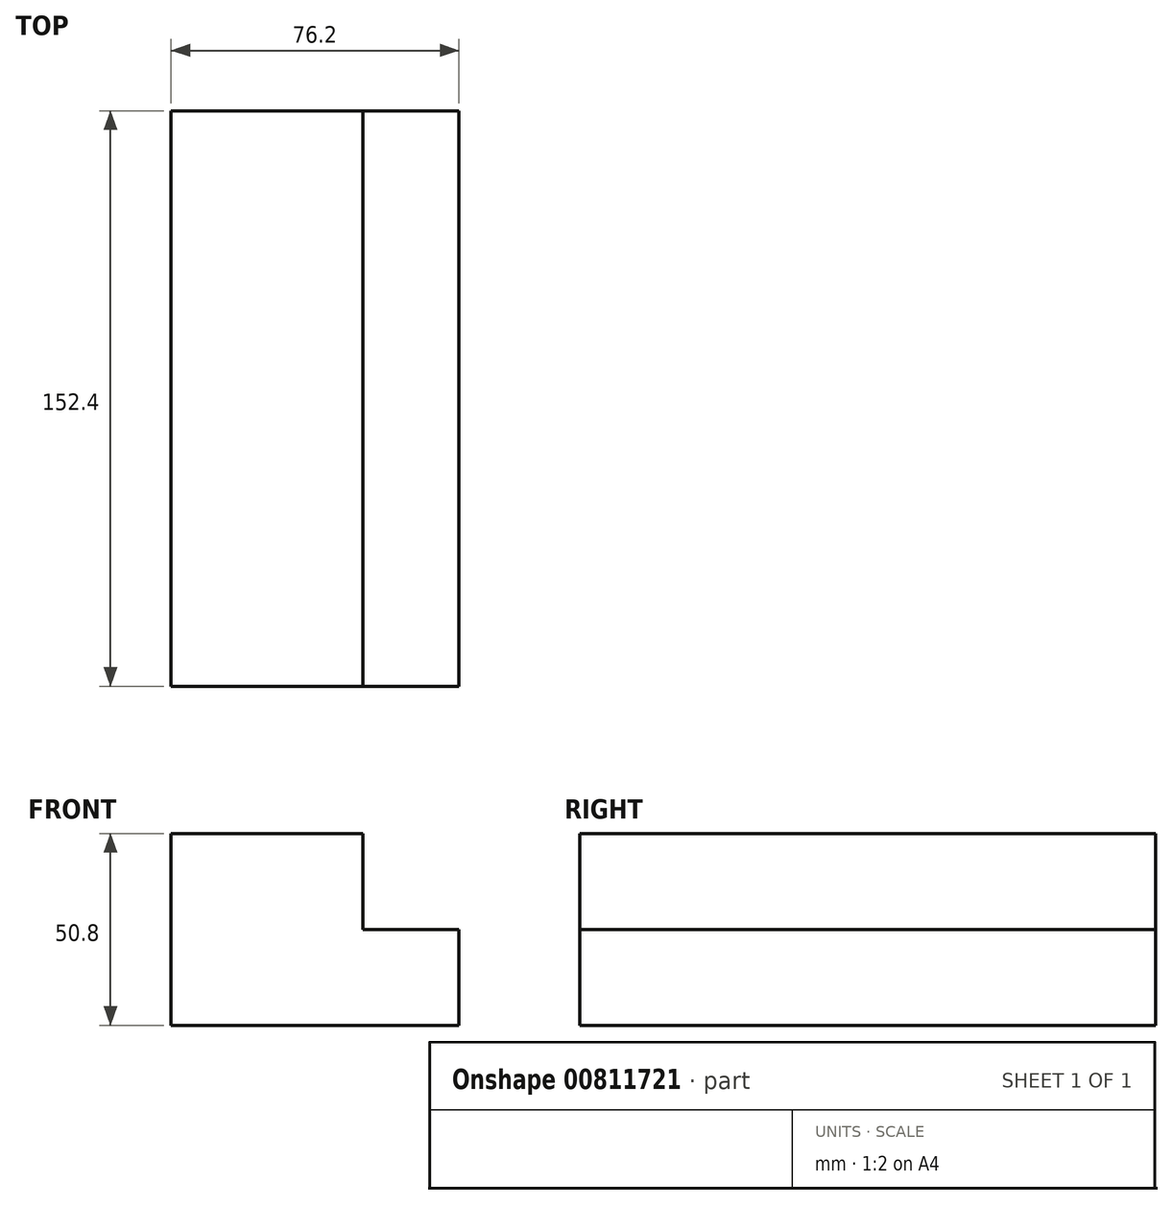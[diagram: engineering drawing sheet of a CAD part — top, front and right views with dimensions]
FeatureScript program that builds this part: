
annotation { "Feature Type Name" : "Feature", "Feature Type Description" : "" }
export const myFeature = defineFeature(function(context is Context, id is Id, definition is map)
    precondition{}
    {
        {
            var Q0;
            Q0=qCreatedBy(makeId("Front.planeOp"),FACE);
            var sketch = newSketch(context, id + "F0", { "sketchPlane" : qUnion([Q0])});
            skLineSegment(sketch, "E0", {"start": v(0, 0) * mm, "end": v(-76.2, 0) * mm});
            skLineSegment(sketch, "E1", {"start": v(-76.2, 0) * mm, "end": v(-76.2, 50.8) * mm});
            skLineSegment(sketch, "E2", {"start": v(-76.2, 50.8) * mm, "end": v(-25.4, 50.8) * mm});
            skLineSegment(sketch, "E3", {"start": v(-25.4, 50.8) * mm, "end": v(-25.4, 25.4) * mm});
            skLineSegment(sketch, "E4", {"start": v(-25.4, 25.4) * mm, "end": v(0, 25.4) * mm});
            skLineSegment(sketch, "E5", {"start": v(0, 25.4) * mm, "end": v(0, 0) * mm});
            skSolve(sketch);
        }
        {
            var Q0;
            Q0=makeQuery(id+"F0.imprint","IMPRINT",FACE,{"disambiguationData":[TD([[makeQuery(id+"F0.imprint","IMPRINT",EDGE,{"derivedFrom":sQuery(id+"F0.wireOp",EDGE,"E0")}),-1.0]])]});
            extrude(context, id + "F1", {"entities" : qUnion([Q0]), "depth" : 152.4 * mm, "offsetDistance" : 25.4 * mm});
        }
    });
